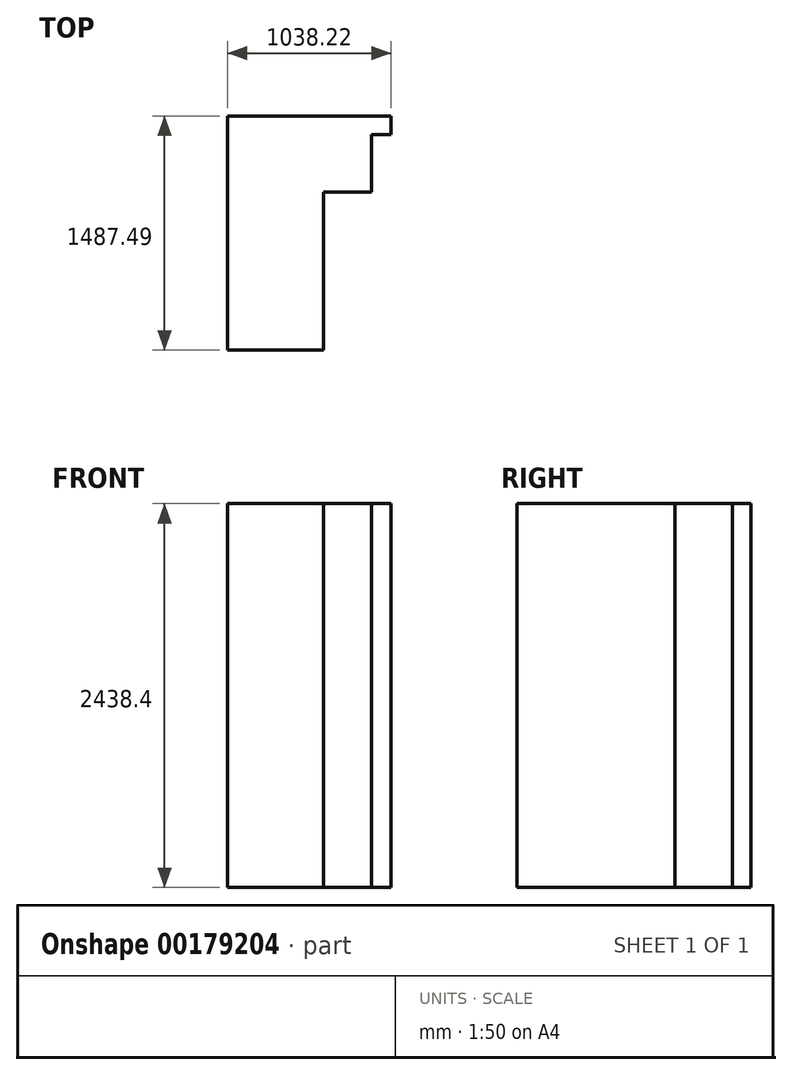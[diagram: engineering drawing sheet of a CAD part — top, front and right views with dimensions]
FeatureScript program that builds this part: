
annotation { "Feature Type Name" : "Feature", "Feature Type Description" : "" }
export const myFeature = defineFeature(function(context is Context, id is Id, definition is map)
    precondition{}
    {
        {
            var Q0;
            Q0=qCreatedBy(makeId("Top.planeOp"),FACE);
            var sketch = newSketch(context, id + "F0", { "sketchPlane" : qUnion([Q0])});
            skLineSegment(sketch, "E0", {"start": v(0, 0) * mm, "end": v(0, -1487.49) * mm});
            skLineSegment(sketch, "E1", {"start": v(0, -1487.49) * mm, "end": v(609.6, -1487.49) * mm});
            skLineSegment(sketch, "E2", {"start": v(609.6, -1487.49) * mm, "end": v(609.6, -484.19) * mm});
            skLineSegment(sketch, "E3", {"start": v(609.6, -484.19) * mm, "end": v(914.4, -484.19) * mm});
            skLineSegment(sketch, "E4", {"start": v(914.4, -484.19) * mm, "end": v(914.4, -117.47) * mm});
            skLineSegment(sketch, "E5", {"start": v(914.4, -117.47) * mm, "end": v(1038.23, -117.47) * mm});
            skLineSegment(sketch, "E6", {"start": v(1038.23, -117.47) * mm, "end": v(1038.23, 0) * mm});
            skLineSegment(sketch, "E7", {"start": v(1038.23, 0) * mm, "end": v(0, 0) * mm});
            skSolve(sketch);
        }
        {
            var Q0;
            Q0=makeQuery(id+"F0.imprint","IMPRINT",FACE,{"disambiguationData":[TD([[makeQuery(id+"F0.imprint","IMPRINT",EDGE,{"derivedFrom":sQuery(id+"F0.wireOp",EDGE,"E0")}),1.0]])]});
            extrude(context, id + "F1", {"entities" : qUnion([Q0]), "depth" : 2438.4 * mm});
        }
    });
